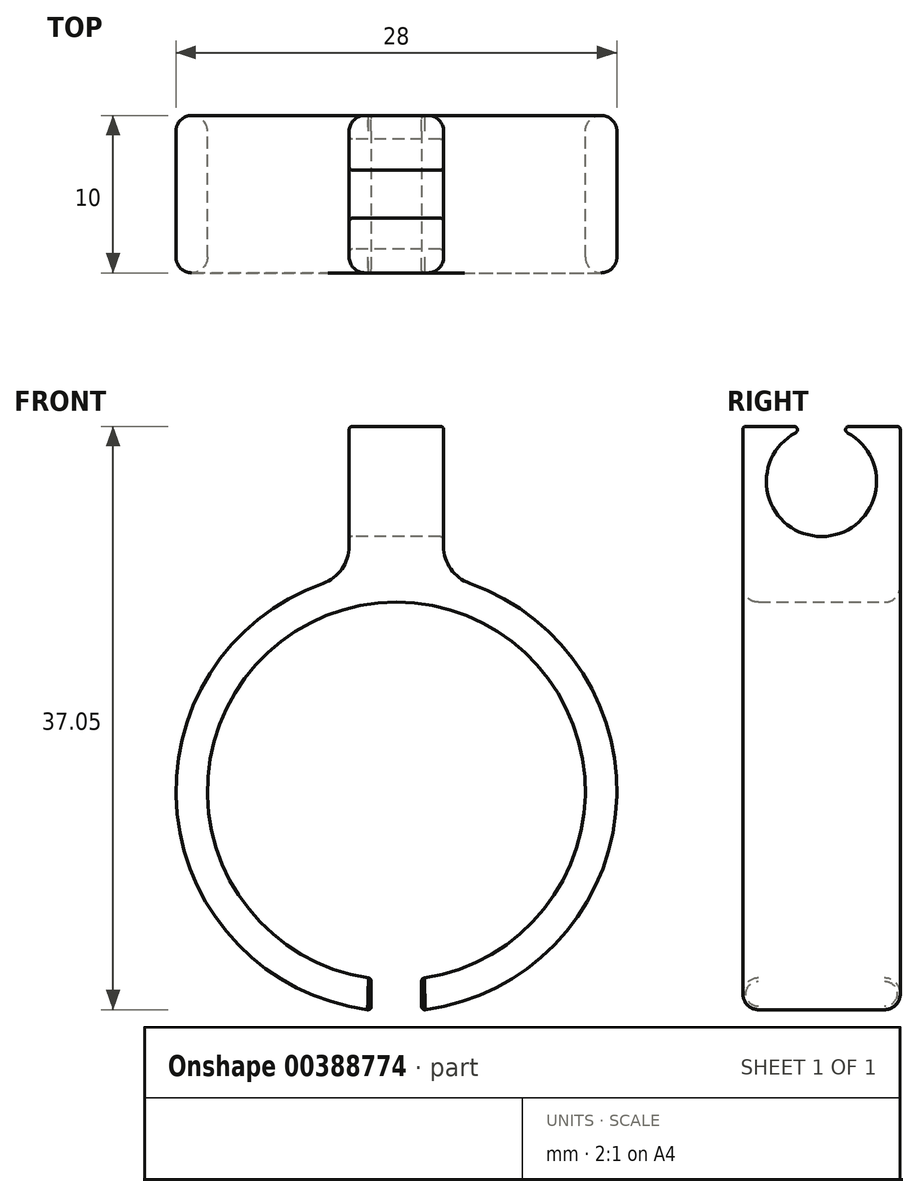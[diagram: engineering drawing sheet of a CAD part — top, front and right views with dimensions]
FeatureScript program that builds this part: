
annotation { "Feature Type Name" : "Feature", "Feature Type Description" : "" }
export const myFeature = defineFeature(function(context is Context, id is Id, definition is map)
    precondition{}
    {
        {
            var Q0;
            Q0=qCreatedBy(makeId("Front.planeOp"),FACE);
            var sketch = newSketch(context, id + "F0", { "sketchPlane" : qUnion([Q0])});
            skArc(sketch, "E0", {"start": v(1.6, -11.9) * mm, "mid": v(0, 12) * mm, "end": v(-1.6, -11.9) * mm});
            skArc(sketch, "E1.0", {"start": v(1.6, -13.9) * mm, "mid": v(13.98, -0.7) * mm, "end": v(3, 13.67) * mm});
            skLineSegment(sketch, "E2", {"start": v(0, 15.17) * mm, "end": v(0, -17.07) * mm, "construction": true});
            skLineSegment(sketch, "E3", {"start": v(-1.6, -11.9) * mm, "end": v(-1.6, -13.9) * mm});
            skLineSegment(sketch, "E4", {"start": v(1.6, -11.9) * mm, "end": v(1.6, -13.9) * mm});
            skLineSegment(sketch, "E5.bottom", {"start": v(-3, 15.17) * mm, "end": v(3, 15.17) * mm});
            skLineSegment(sketch, "E5.left", {"start": v(-3, 15.17) * mm, "end": v(-3, 13.67) * mm});
            skLineSegment(sketch, "E5.right", {"start": v(3, 15.17) * mm, "end": v(3, 13.67) * mm});
            skArc(sketch, "E6.trimOffspring", {"start": v(-3, 13.67) * mm, "mid": v(-13.98, -0.7) * mm, "end": v(-1.6, -13.9) * mm});
            skLineSegment(sketch, "E7", {"start": v(-13.34, 13.67) * mm, "end": v(13.22, 13.67) * mm, "construction": true});
            skSolve(sketch);
        }
        {
            var Q0;
            Q0=makeQuery(id+"F0.imprint","IMPRINT",FACE,{"disambiguationData":[TD([[makeQuery(id+"F0.imprint","IMPRINT",EDGE,{"derivedFrom":sQuery(id+"F0.wireOp",EDGE,"E0")}),-1.0]])]});
            var Q1;
            Q1 = qSketchRegion(id + "F2", true);
            extrude(context, id + "F1", {"entities" : qUnion([Q0, Q1]), "endBound" : BoundingType.SYMMETRIC, "depth" : 10 * mm});
        }
        {
            var Q0;
            Q0=qCreatedBy(makeId("Right.planeOp"),FACE);
            var sketch = newSketch(context, id + "F2", { "sketchPlane" : qUnion([Q0])});
            skArc(sketch, "E8", {"start": v(-1.65, 22.76) * mm, "mid": v(0, 16.17) * mm, "end": v(1.65, 22.76) * mm});
            skPoint(sketch, "E9.visualSharp", {"position": v(-8, 13.24) * mm});
            skPoint(sketch, "E10.visualSharp", {"position": v(8, 13.24) * mm});
            skLineSegment(sketch, "E11.bottom", {"start": v(-5, 15.17) * mm, "end": v(5, 15.17) * mm});
            skLineSegment(sketch, "E11.top", {"start": v(-5, 23.17) * mm, "end": v(-1.75, 23.17) * mm});
            skLineSegment(sketch, "E11.left", {"start": v(-5, 15.17) * mm, "end": v(-5, 23.17) * mm});
            skLineSegment(sketch, "E11.right", {"start": v(5, 15.17) * mm, "end": v(5, 23.17) * mm});
            skLineSegment(sketch, "E12.trimOffspring", {"start": v(1.75, 23.17) * mm, "end": v(5, 23.17) * mm});
            skArc(sketch, "E13", {"start": v(-1.65, 22.76) * mm, "mid": v(-1.54, 23) * mm, "end": v(-1.75, 23.17) * mm});
            skArc(sketch, "E14", {"start": v(1.75, 23.17) * mm, "mid": v(1.54, 23) * mm, "end": v(1.65, 22.76) * mm});
            skSolve(sketch);
        }
        {
            var Q0;
            Q0=makeQuery(id+"F2.imprint","IMPRINT",FACE,{"disambiguationData":[TD([[makeQuery(id+"F2.imprint","IMPRINT",EDGE,{"derivedFrom":sQuery(id+"F2.wireOp",EDGE,"E8")}),-1.0]])]});
            var Q1;
            Q1=makeQuery(id+"F1.opExtrude","SWEPT_FACE",FACE,{"disambiguationData":[OSD([sQuery(id+"F0.wireOp",EDGE,"E5.right")])]});
            var Q2;
            Q2=makeQuery(id+"F1.opExtrude","SWEPT_FACE",FACE,{"disambiguationData":[OSD([sQuery(id+"F0.wireOp",EDGE,"E5.left")])]});
            extrude(context, id + "F3", {"entities" : qUnion([Q0]), "operationType" : NewBodyOperationType.ADD, "endBound" : BoundingType.UP_TO_SURFACE, "endBoundEntityFace" : qUnion([Q1]), "depth" : 5 * mm, "hasSecondDirection" : true, "secondDirectionBound" : SecondDirectionBoundingType.UP_TO_SURFACE, "secondDirectionOppositeDirection" : true, "secondDirectionBoundEntityFace" : qUnion([Q2]), "secondDirectionDepth" : 25 * mm});
        }
        {
            var Q0;
            Q0=makeQuery(id+"F1.opExtrude","SWEPT_EDGE",EDGE,{"disambiguationData":[OSD([sQuery(id+"F0.wireOp",EDGE,"E1.0"),sQuery(id+"F0.wireOp",EDGE,"E5.right")])]});
            var Q1;
            Q1=makeQuery(id+"F1.opExtrude","SWEPT_EDGE",EDGE,{"disambiguationData":[OSD([sQuery(id+"F0.wireOp",EDGE,"E5.left"),sQuery(id+"F0.wireOp",EDGE,"E6.trimOffspring")])]});
            fillet(context, id + "F4", {"entities" : qUnion([Q0, Q1]), "radius" : 2.5 * mm, "tangentPropagation" : true, "allowEdgeOverflow" : false});
        }
        {
            var Q0;
            Q0=makeQuery(id+"F1.opExtrude","CAP_EDGE",EDGE,{"disambiguationData":[OSD([sQuery(id+"F0.wireOp",EDGE,"E0")])],"isStart":true});
            var Q1;
            Q1=makeQuery(id+"F1.opExtrude","CAP_EDGE",EDGE,{"disambiguationData":[OSD([sQuery(id+"F0.wireOp",EDGE,"E6.trimOffspring")])],"isStart":true});
            var Q2;
            Q2=makeQuery(id+"F1.opExtrude","CAP_EDGE",EDGE,{"disambiguationData":[OSD([sQuery(id+"F0.wireOp",EDGE,"E6.trimOffspring")])],"isStart":false});
            var Q3;
            Q3=makeQuery(id+"F1.opExtrude","CAP_EDGE",EDGE,{"disambiguationData":[OSD([sQuery(id+"F0.wireOp",EDGE,"E0")])],"isStart":false});
            var Q4;
            Q4=makeQuery(id+"F1.opExtrude","CAP_EDGE",EDGE,{"disambiguationData":[OSD([sQuery(id+"F0.wireOp",EDGE,"E1.0")])],"isStart":false});
            var Q5;
            Q5=makeQuery(id+"F1.opExtrude","CAP_EDGE",EDGE,{"disambiguationData":[OSD([sQuery(id+"F0.wireOp",EDGE,"E1.0")])],"isStart":true});
            var Q6;
            Q6=makeQuery(id+"F1.opExtrude","CAP_EDGE",EDGE,{"disambiguationData":[OSD([sQuery(id+"F0.wireOp",EDGE,"E5.bottom")])],"isStart":false});
            var Q7;
            Q7=makeQuery(id+"F1.opExtrude","CAP_EDGE",EDGE,{"disambiguationData":[OSD([sQuery(id+"F0.wireOp",EDGE,"E5.bottom")])],"isStart":true});
            var Q8;
            Q8=makeQuery(id+"F3.opExtrude","TWEAK_EDGE",EDGE,{"derivedFrom":[makeQuery(id+"F2.imprint","IMPRINT",EDGE,{"derivedFrom":sQuery(id+"F2.wireOp",EDGE,"E11.top")}),makeQuery(id+"F2.imprint","IMPRINT",EDGE,{"derivedFrom":sQuery(id+"F2.wireOp",EDGE,"E11.left")})]});
            var Q9;
            Q9=makeQuery(id+"F3.opExtrude","TWEAK_EDGE",EDGE,{"derivedFrom":[makeQuery(id+"F2.imprint","IMPRINT",EDGE,{"derivedFrom":sQuery(id+"F2.wireOp",EDGE,"E11.right")}),makeQuery(id+"F2.imprint","IMPRINT",EDGE,{"derivedFrom":sQuery(id+"F2.wireOp",EDGE,"E12.trimOffspring")})]});
            fillet(context, id + "F5", {"entities" : qUnion([Q0, Q1, Q2, Q3, Q4, Q5, Q6, Q7, Q8, Q9]), "radius" : 1 * mm, "tangentPropagation" : true, "allowEdgeOverflow" : false});
        }
        {
            var Q0;
            Q0=makeQuery(id+"F3.opExtrude","CAP_EDGE",EDGE,{"disambiguationData":[OSD([sQuery(id+"F2.wireOp",EDGE,"E8")])],"isStart":false});
            var Q1;
            Q1=makeQuery(id+"F3.opExtrude","CAP_EDGE",EDGE,{"disambiguationData":[OSD([sQuery(id+"F2.wireOp",EDGE,"E8")])],"isStart":true});
            var Q2;
            Q2=makeQuery(id+"F3.opExtrude","TWEAK_EDGE",EDGE,{"derivedFrom":[makeQuery(id+"F2.imprint","IMPRINT",EDGE,{"derivedFrom":sQuery(id+"F2.wireOp",EDGE,"E11.bottom")}),makeQuery(id+"F2.imprint","IMPRINT",EDGE,{"derivedFrom":sQuery(id+"F2.wireOp",EDGE,"E11.left")})]});
            var Q3;
            Q3=makeQuery(id+"F3.opExtrude","TWEAK_EDGE",EDGE,{"derivedFrom":[makeQuery(id+"F2.imprint","IMPRINT",EDGE,{"derivedFrom":sQuery(id+"F2.wireOp",EDGE,"E11.bottom")}),makeQuery(id+"F2.imprint","IMPRINT",EDGE,{"derivedFrom":sQuery(id+"F2.wireOp",EDGE,"E11.right")})]});
            var Q4;
            Q4=makeQuery(id+"F1.opExtrude","SWEPT_FACE",FACE,{"disambiguationData":[OSD([sQuery(id+"F0.wireOp",EDGE,"E3")])]});
            var Q5;
            Q5=makeQuery(id+"F1.opExtrude","SWEPT_FACE",FACE,{"disambiguationData":[OSD([sQuery(id+"F0.wireOp",EDGE,"E4")])]});
            fillet(context, id + "F6", {"entities" : qUnion([Q0, Q1, Q2, Q3, Q4, Q5]), "radius" : 0.2 * mm, "tangentPropagation" : true, "allowEdgeOverflow" : false});
        }
    });
